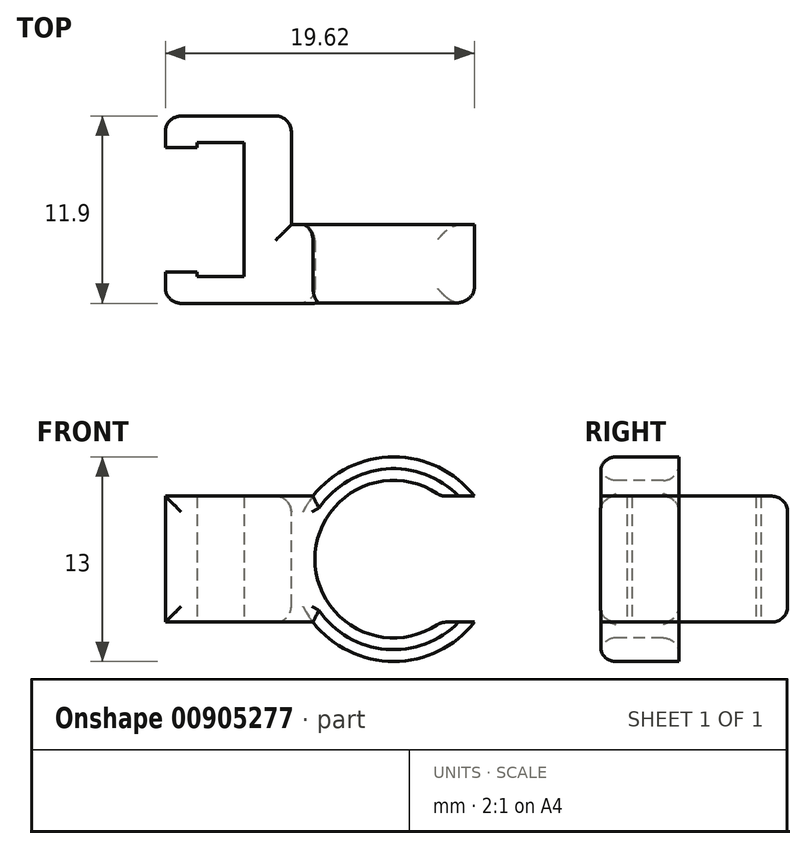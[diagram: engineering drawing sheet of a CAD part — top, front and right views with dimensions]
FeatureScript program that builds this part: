
annotation { "Feature Type Name" : "Feature", "Feature Type Description" : "" }
export const myFeature = defineFeature(function(context is Context, id is Id, definition is map)
    precondition{}
    {
        {
            var Q0;
            Q0=qCreatedBy(makeId("Top.planeOp"),FACE);
            var sketch = newSketch(context, id + "F0", { "sketchPlane" : qUnion([Q0])});
            skLineSegment(sketch, "E0", {"start": v(0, 0) * mm, "end": v(-8, 0) * mm});
            skLineSegment(sketch, "E1", {"start": v(-8, 0) * mm, "end": v(-8, 2) * mm});
            skLineSegment(sketch, "E2", {"start": v(-8, 2) * mm, "end": v(-6, 2) * mm});
            skLineSegment(sketch, "E3", {"start": v(-6, 2) * mm, "end": v(-6, 1.7) * mm});
            skLineSegment(sketch, "E4", {"start": v(-6, 1.7) * mm, "end": v(-3, 1.7) * mm});
            skLineSegment(sketch, "E5", {"start": v(-3, 1.7) * mm, "end": v(-3, 10.2) * mm});
            skLineSegment(sketch, "E6", {"start": v(-3, 10.2) * mm, "end": v(-6, 10.2) * mm});
            skLineSegment(sketch, "E7", {"start": v(-6, 10.2) * mm, "end": v(-6, 9.9) * mm});
            skLineSegment(sketch, "E8", {"start": v(-6, 9.9) * mm, "end": v(-8, 9.9) * mm});
            skLineSegment(sketch, "E9", {"start": v(-8, 9.9) * mm, "end": v(-8, 11.9) * mm});
            skLineSegment(sketch, "E10", {"start": v(-8, 11.9) * mm, "end": v(0, 11.9) * mm});
            skLineSegment(sketch, "E11", {"start": v(0, 11.9) * mm, "end": v(0, 0) * mm});
            skSolve(sketch);
        }
        {
            var Q0;
            Q0=makeQuery(id+"F0.imprint","IMPRINT",FACE,{"disambiguationData":[TD([[makeQuery(id+"F0.imprint","IMPRINT",EDGE,{"derivedFrom":sQuery(id+"F0.wireOp",EDGE,"E0")}),-1.0]])]});
            extrude(context, id + "F1", {"entities" : qUnion([Q0]), "depth" : 8 * mm, "offsetDistance" : 25 * mm});
        }
        {
            var Q0;
            Q0=qCreatedBy(makeId("Front.planeOp"),FACE);
            var sketch = newSketch(context, id + "F2", { "sketchPlane" : qUnion([Q0])});
            skLineSegment(sketch, "E12", {"start": v(0, 4) * mm, "end": v(0, 4) * mm});
            skLineSegment(sketch, "E13", {"start": v(0, 4) * mm, "end": v(6.5, 4) * mm, "construction": true});
            skCircle(sketch, "E14", {"center": v(6.5, 4) * mm, "radius": 5 * mm});
            skCircle(sketch, "E15", {"center": v(6.5, 4) * mm, "radius": 6.5 * mm});
            skLineSegment(sketch, "E16", {"start": v(9.5, 8) * mm, "end": v(11.62, 8) * mm});
            skLineSegment(sketch, "E17.MirrorCS", {"start": v(9.5, 0) * mm, "end": v(11.62, 0) * mm});
            skLineSegment(sketch, "E18", {"start": v(0, 0) * mm, "end": v(1.38, 0) * mm});
            skLineSegment(sketch, "E19.MirrorCS", {"start": v(0, 8) * mm, "end": v(1.38, 8) * mm});
            skLineSegment(sketch, "E20", {"start": v(0, 0) * mm, "end": v(0, 8) * mm});
            skSolve(sketch);
        }
        {
            var Q0;
            {var subQ0=sQuery(id+"F2.wireOp",EDGE,"E16");Q0=makeQuery(id+"F2.imprint","IMPRINT",FACE,{"disambiguationData":[TD([[makeQuery(id+"F2.imprint","IMPRINT",EDGE,{"derivedFrom":subQ0}),1.0]])]});}
            var Q1;
            {var subQ0=sQuery(id+"F2.wireOp",EDGE,"E18");Q1=makeQuery(id+"F2.imprint","IMPRINT",FACE,{"disambiguationData":[TD([[makeQuery(id+"F2.imprint","IMPRINT",EDGE,{"derivedFrom":subQ0}),1.0]])]});}
            var Q2;
            {var subQ0=sQuery(id+"F2.wireOp",EDGE,"E19.MirrorCS");Q2=makeQuery(id+"F2.imprint","IMPRINT",FACE,{"disambiguationData":[TD([[makeQuery(id+"F2.imprint","IMPRINT",EDGE,{"derivedFrom":subQ0}),-1.0]])]});}
            extrude(context, id + "F3", {"entities" : qUnion([Q0, Q1, Q2]), "operationType" : NewBodyOperationType.ADD, "depth" : -5 * mm, "offsetDistance" : 25 * mm});
        }
        {
            var Q0;
            Q0=makeQuery(id+"F1.opExtrude","SWEPT_FACE",FACE,{"disambiguationData":[OSD([sQuery(id+"F0.wireOp",EDGE,"E10")])]});
            var Q1;
            Q1=makeQuery(id+"F3.boolean.opBoolean","MERGE",EDGE,{"derivedFrom":[makeQuery(id+"F1.opExtrude","CAP_EDGE",EDGE,{"disambiguationData":[OSD([sQuery(id+"F0.wireOp",EDGE,"E0")])],"isStart":true}),makeQuery(id+"F3.opExtrude","CAP_EDGE",EDGE,{"disambiguationData":[OSD([sQuery(id+"F2.wireOp",EDGE,"E18")])],"isStart":true})]});
            var Q2;
            {var subQ0=sQuery(id+"F2.wireOp",EDGE,"E15");Q2=makeQuery(id+"F3.opExtrude","CAP_EDGE",EDGE,{"disambiguationData":[OSD([subQ0]),TDD([makeQuery(id+"F2.imprint","IMPRINT",EDGE,{"disambiguationData":[TD([[makeQuery(id+"F2.imprint","INTERSECT",VERTEX,{"derivedFrom":[subQ0,sQuery(id+"F2.wireOp",EDGE,"E17.MirrorCS")]}),1.0]])],"derivedFrom":subQ0})])],"isStart":true});}
            var Q3;
            {var subQ0=sQuery(id+"F2.wireOp",EDGE,"E15");Q3=makeQuery(id+"F3.opExtrude","CAP_EDGE",EDGE,{"disambiguationData":[OSD([subQ0]),TDD([makeQuery(id+"F2.imprint","IMPRINT",EDGE,{"disambiguationData":[TD([[makeQuery(id+"F2.imprint","INTERSECT",VERTEX,{"derivedFrom":[subQ0,sQuery(id+"F2.wireOp",EDGE,"E16")]}),-1.0]])],"derivedFrom":subQ0})])],"isStart":true});}
            var Q4;
            Q4=makeQuery(id+"F3.boolean.opBoolean","MERGE",EDGE,{"derivedFrom":[makeQuery(id+"F1.opExtrude","CAP_EDGE",EDGE,{"disambiguationData":[OSD([sQuery(id+"F0.wireOp",EDGE,"E0")])],"isStart":false}),makeQuery(id+"F3.opExtrude","CAP_EDGE",EDGE,{"disambiguationData":[OSD([sQuery(id+"F2.wireOp",EDGE,"E19.MirrorCS")])],"isStart":true})]});
            var Q5;
            Q5=makeQuery(id+"F1.opExtrude","SWEPT_EDGE",EDGE,{"disambiguationData":[OSD([sQuery(id+"F0.wireOp",EDGE,"E0"),sQuery(id+"F0.wireOp",EDGE,"E1")])]});
            var Q6;
            Q6=makeQuery(id+"F3.opExtrude","CAP_EDGE",EDGE,{"disambiguationData":[OSD([sQuery(id+"F2.wireOp",EDGE,"E14")])],"isStart":true});
            var Q7;
            Q7=makeQuery(id+"F1.opExtrude","CAP_EDGE",EDGE,{"disambiguationData":[OSD([sQuery(id+"F0.wireOp",EDGE,"E11")])],"isStart":false});
            var Q8;
            Q8=makeQuery(id+"F1.opExtrude","CAP_EDGE",EDGE,{"disambiguationData":[OSD([sQuery(id+"F0.wireOp",EDGE,"E11")])],"isStart":true});
            var Q9;
            Q9=makeQuery(id+"F3.opExtrude","CAP_EDGE",EDGE,{"disambiguationData":[OSD([sQuery(id+"F2.wireOp",EDGE,"E19.MirrorCS")])],"isStart":false});
            var Q10;
            Q10=makeQuery(id+"F3.opExtrude","CAP_EDGE",EDGE,{"disambiguationData":[OSD([sQuery(id+"F2.wireOp",EDGE,"E18")])],"isStart":false});
            var Q11;
            Q11=makeQuery(id+"F3.opExtrude","SWEPT_FACE",FACE,{"disambiguationData":[OSD([sQuery(id+"F2.wireOp",EDGE,"E14")])]});
            fillet(context, id + "F4", {"entities" : qUnion([Q0, Q1, Q2, Q3, Q4, Q5, Q6, Q7, Q8, Q9, Q10, Q11]), "radius" : 1 * mm, "tangentPropagation" : true, "allowEdgeOverflow" : false});
        }
    });
